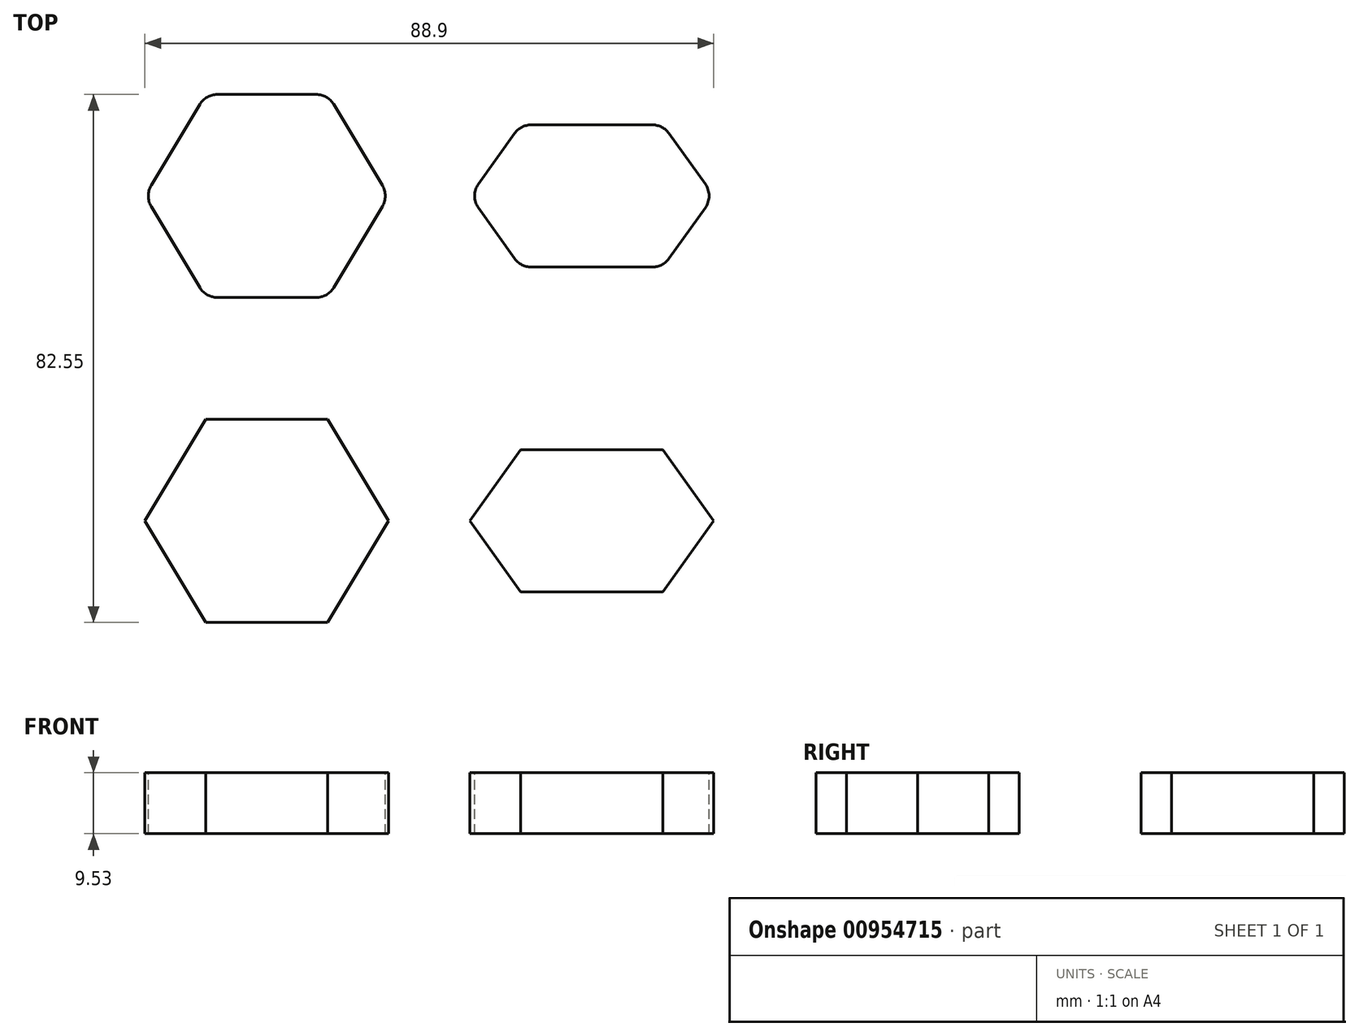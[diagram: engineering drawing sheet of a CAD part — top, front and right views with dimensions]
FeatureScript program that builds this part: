
annotation { "Feature Type Name" : "Feature", "Feature Type Description" : "" }
export const myFeature = defineFeature(function(context is Context, id is Id, definition is map)
    precondition{}
    {
        {
            var Q0;
            Q0=qCreatedBy(makeId("Top.planeOp"),FACE);
            var sketch = newSketch(context, id + "F0", { "sketchPlane" : qUnion([Q0])});
            skLineSegment(sketch, "E0", {"start": v(-9.53, 34.93) * mm, "end": v(-19.05, 50.8) * mm});
            skLineSegment(sketch, "E1", {"start": v(-19.05, 50.8) * mm, "end": v(-9.52, 66.68) * mm});
            skLineSegment(sketch, "E2", {"start": v(-9.53, 66.68) * mm, "end": v(9.53, 66.68) * mm});
            skLineSegment(sketch, "E3", {"start": v(9.53, 66.68) * mm, "end": v(19.05, 50.8) * mm});
            skLineSegment(sketch, "E4", {"start": v(19.05, 50.8) * mm, "end": v(9.52, 34.92) * mm});
            skLineSegment(sketch, "E5", {"start": v(9.53, 34.93) * mm, "end": v(-9.53, 34.93) * mm});
            skLineSegment(sketch, "E6", {"start": v(39.69, 39.69) * mm, "end": v(31.75, 50.8) * mm});
            skLineSegment(sketch, "E7", {"start": v(31.75, 50.8) * mm, "end": v(39.69, 61.91) * mm});
            skLineSegment(sketch, "E8", {"start": v(39.69, 61.91) * mm, "end": v(61.91, 61.91) * mm});
            skLineSegment(sketch, "E9", {"start": v(61.91, 61.91) * mm, "end": v(69.85, 50.8) * mm});
            skLineSegment(sketch, "E10", {"start": v(69.85, 50.8) * mm, "end": v(61.91, 39.69) * mm});
            skLineSegment(sketch, "E11", {"start": v(61.91, 39.69) * mm, "end": v(39.69, 39.69) * mm});
            skLineSegment(sketch, "E12", {"start": v(-9.52, -15.88) * mm, "end": v(-19.05, 0) * mm});
            skLineSegment(sketch, "E13", {"start": v(-19.05, 0) * mm, "end": v(-9.53, 15.87) * mm});
            skLineSegment(sketch, "E14", {"start": v(-9.52, 15.88) * mm, "end": v(9.53, 15.88) * mm});
            skLineSegment(sketch, "E15", {"start": v(9.52, 15.88) * mm, "end": v(19.05, 0) * mm});
            skLineSegment(sketch, "E16", {"start": v(19.05, 0) * mm, "end": v(9.53, -15.87) * mm});
            skLineSegment(sketch, "E17", {"start": v(9.52, -15.88) * mm, "end": v(-9.53, -15.88) * mm});
            skLineSegment(sketch, "E18", {"start": v(39.69, -11.11) * mm, "end": v(31.75, 0) * mm});
            skLineSegment(sketch, "E19", {"start": v(31.75, 0) * mm, "end": v(39.69, 11.11) * mm});
            skLineSegment(sketch, "E20", {"start": v(39.69, 11.11) * mm, "end": v(61.91, 11.11) * mm});
            skLineSegment(sketch, "E21", {"start": v(61.91, 11.11) * mm, "end": v(69.85, 0) * mm});
            skLineSegment(sketch, "E22", {"start": v(69.85, 0) * mm, "end": v(61.91, -11.11) * mm});
            skLineSegment(sketch, "E23", {"start": v(61.91, -11.11) * mm, "end": v(39.69, -11.11) * mm});
            skSolve(sketch);
        }
        {
            var Q0;
            Q0=qSketchRegion(id+"F0",true);
            var Q1;
            Q1=makeQuery(id+"F0.imprint","IMPRINT",FACE,{"disambiguationData":[TD([[makeQuery(id+"F0.imprint","IMPRINT",EDGE,{"derivedFrom":sQuery(id+"F0.wireOp",EDGE,"8e1de53d-4f07-4b73-9790-9e71334486fa")}),-1.0]])]});
            var Q2;
            Q2=makeQuery(id+"F0.imprint","IMPRINT",FACE,{"disambiguationData":[TD([[makeQuery(id+"F0.imprint","IMPRINT",EDGE,{"derivedFrom":sQuery(id+"F0.wireOp",EDGE,"fb696887-fdbb-4c20-8097-e49d6d1a9a27")}),-1.0]])]});
            var Q3;
            Q3=makeQuery(id+"F0.imprint","IMPRINT",FACE,{"disambiguationData":[TD([[makeQuery(id+"F0.imprint","IMPRINT",EDGE,{"derivedFrom":sQuery(id+"F0.wireOp",EDGE,"d657898a-c649-4e48-968d-d8c73fd1a2c2")}),-1.0]])]});
            var Q4;
            Q4=makeQuery(id+"F0.imprint","IMPRINT",FACE,{"disambiguationData":[TD([[makeQuery(id+"F0.imprint","IMPRINT",EDGE,{"derivedFrom":sQuery(id+"F0.wireOp",EDGE,"f5a97981-d887-4c3c-8f6c-bc2508b50226")}),-1.0]])]});
            extrude(context, id + "F1", {"entities" : qUnion([Q0, Q1, Q2, Q3, Q4]), "oppositeDirection" : true, "depth" : 9.52 * mm, "offsetDistance" : 25.4 * mm});
        }
        {
            var Q0;
            Q0=makeQuery(id+"F1.opExtrude","SWEPT_EDGE",EDGE,{"disambiguationData":[OSD([sQuery(id+"F0.wireOp",EDGE,"E0"),sQuery(id+"F0.wireOp",EDGE,"E1")])]});
            var Q1;
            Q1=makeQuery(id+"F1.opExtrude","SWEPT_EDGE",EDGE,{"disambiguationData":[OSD([sQuery(id+"F0.wireOp",EDGE,"E0"),sQuery(id+"F0.wireOp",EDGE,"E5")])]});
            var Q2;
            Q2=makeQuery(id+"F1.opExtrude","SWEPT_EDGE",EDGE,{"disambiguationData":[OSD([sQuery(id+"F0.wireOp",EDGE,"E6"),sQuery(id+"F0.wireOp",EDGE,"E7")])]});
            var Q3;
            Q3=makeQuery(id+"F1.opExtrude","SWEPT_EDGE",EDGE,{"disambiguationData":[OSD([sQuery(id+"F0.wireOp",EDGE,"E3"),sQuery(id+"F0.wireOp",EDGE,"E4")])]});
            var Q4;
            Q4=makeQuery(id+"F1.opExtrude","SWEPT_EDGE",EDGE,{"disambiguationData":[OSD([sQuery(id+"F0.wireOp",EDGE,"E4"),sQuery(id+"F0.wireOp",EDGE,"E5")])]});
            var Q5;
            Q5=makeQuery(id+"F1.opExtrude","SWEPT_EDGE",EDGE,{"disambiguationData":[OSD([sQuery(id+"F0.wireOp",EDGE,"E2"),sQuery(id+"F0.wireOp",EDGE,"E3")])]});
            var Q6;
            Q6=makeQuery(id+"F1.opExtrude","SWEPT_EDGE",EDGE,{"disambiguationData":[OSD([sQuery(id+"F0.wireOp",EDGE,"E1"),sQuery(id+"F0.wireOp",EDGE,"E2")])]});
            var Q7;
            Q7=makeQuery(id+"F1.opExtrude","SWEPT_EDGE",EDGE,{"disambiguationData":[OSD([sQuery(id+"F0.wireOp",EDGE,"E7"),sQuery(id+"F0.wireOp",EDGE,"E8")])]});
            var Q8;
            Q8=makeQuery(id+"F1.opExtrude","SWEPT_EDGE",EDGE,{"disambiguationData":[OSD([sQuery(id+"F0.wireOp",EDGE,"E8"),sQuery(id+"F0.wireOp",EDGE,"E9")])]});
            var Q9;
            Q9=makeQuery(id+"F1.opExtrude","SWEPT_EDGE",EDGE,{"disambiguationData":[OSD([sQuery(id+"F0.wireOp",EDGE,"E9"),sQuery(id+"F0.wireOp",EDGE,"E10")])]});
            var Q10;
            Q10=makeQuery(id+"F1.opExtrude","SWEPT_EDGE",EDGE,{"disambiguationData":[OSD([sQuery(id+"F0.wireOp",EDGE,"E10"),sQuery(id+"F0.wireOp",EDGE,"E11")])]});
            var Q11;
            Q11=makeQuery(id+"F1.opExtrude","SWEPT_EDGE",EDGE,{"disambiguationData":[OSD([sQuery(id+"F0.wireOp",EDGE,"E6"),sQuery(id+"F0.wireOp",EDGE,"E11")])]});
            fillet(context, id + "F2", {"entities" : qUnion([Q0, Q1, Q2, Q3, Q4, Q5, Q6, Q7, Q8, Q9, Q10, Q11]), "radius" : 3.17 * mm, "tangentPropagation" : true, "allowEdgeOverflow" : false});
        }
    });
